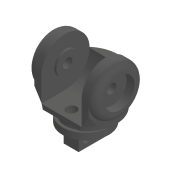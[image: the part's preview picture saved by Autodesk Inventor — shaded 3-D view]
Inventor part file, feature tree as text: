
AUTODESK INVENTOR PART (.ipt)
format: ipt  version: 2020 (Build 240168000, 168)  size: 883,712 bytes
history: native  units: mm
features: sketch x18, extrude x15, mirror x4, plane x4, loft x2, fillet x1, projected_geometry x1, other x1
ambient origin geometry x8: Origin, YZ Plane, XZ Plane, XY Plane, X Axis, Y Axis, Z Axis, Center Point
bodies: Solid1 (feature_tree)
feature tree (46):
  extrude  "Extrusion1"  Depth=1.5mm TaperAngle=0.0deg
  extrude  "Extrusion2"  Depth=1.5mm TaperAngle=0.0deg
  extrude  "Extrusion3"  Depth=1.0mm TaperAngle=0.0deg
  extrude  "Extrusion4"  Depth=12.36mm TaperAngle=0.0deg
  extrude  "Extrusion5"  Depth=1.57mm TaperAngle=0.0deg
  extrude  "Extrusion6"  TaperAngle=0.0deg  [1 undecoded]
  mirror  "Mirror1"
  plane  "Work Plane1"
  loft  "Loft1"
  fillet  "Fillet1"  Radius=5.5mm
  plane  "Work Plane3"
  extrude  "Extrusion7"  Depth=11.0mm
  loft  "Loft2"
  mirror  "Mirror2"
  extrude  "Extrusion8"  Depth=5.12mm
  mirror  "Mirror3"
  extrude  "Extrusion9"  Depth=6.75mm
  mirror  "Mirror4"
  extrude  "Extrusion10"  Depth=2.12mm
  extrude  "Extrusion11"  Depth=3.4mm
  extrude  "Extrusion12"  Depth=3.5mm TaperAngle=0.0deg
  extrude  "Extrusion13"  Depth=0.9mm
  plane  "Work Plane4"
  extrude  "Extrusion14"  Depth=0.486mm
  plane  "Work Plane5"
  extrude  "Extrusion15"  Depth=1.8mm
  sketch  "Sketch2"  dims[d0=10.5mm d1=1.5mm d2=0.0mm]
  sketch  "Sketch3"  dims[d3=9.25mm d4=1.5mm d5=0.0mm]
  sketch  "Sketch4"  dims[d6=13.9mm d7=1.0mm d8=0.0mm]
  sketch  "Sketch6"  dims[d9=5.5mm d10=12.36mm d11=0.0mm]
  projected_geometry  "Projected Loop1"
  sketch  "Sketch7"  dims[d12=1.11mm d13=0.0mm d14=1.57mm d15=0.0mm]
  sketch  "Sketch8"  dims[d16=5.5mm d62=0.0mm d63=90.0deg]
  other  "Image1"
  sketch  "Sketch9"  dims[d64=0.0mm d65=90.0deg d66=1.57mm d69=5.5mm]
  sketch  "Sketch11"  dims[d70=5.5mm d71=11.0mm]
  sketch  "3D Sketch1"
  sketch  "Sketch13"  dims[d72=9.2mm d73=0.0mm d77=0.0mm d78=90.0deg]
  sketch  "Sketch14"  dims[d79=0.0mm d80=90.0deg d81=5.12mm]
  sketch  "Sketch15"  dims[d82=0.5mm d83=0.0mm d84=6.75mm]
  sketch  "Sketch16"  dims[d85=1.8mm d86=0.0mm d87=2.12mm]
  sketch  "Sketch17"  dims[d88=0.0mm d89=0.0mm d90=3.4mm]
  sketch  "Sketch18"  dims[d91=6.6mm d92=3.5mm d93=0.0mm]
  sketch  "Sketch19"  dims[d94=0.486mm d95=0.9mm]
  sketch  "Sketch20"  dims[d96=2.2625mm d97=0.0mm d98=0.486mm]
  sketch  "Sketch21"  dims[d99=0.5625mm d100=1.8mm d101=3.5mm d102=0.0mm d103=27.925268mm d104=2.2mm d105=6.5mm d106=0.0mm d107=3.054326mm d108=2.2mm d109=6.5mm d110=12.5mm d111=0.0mm d112=0.0mm]
note: 1 required parameter value undecoded (feature->parameter linkage not recoverable at this tier; creation-order binding heuristic only, values carry confidence <= 0.55)
